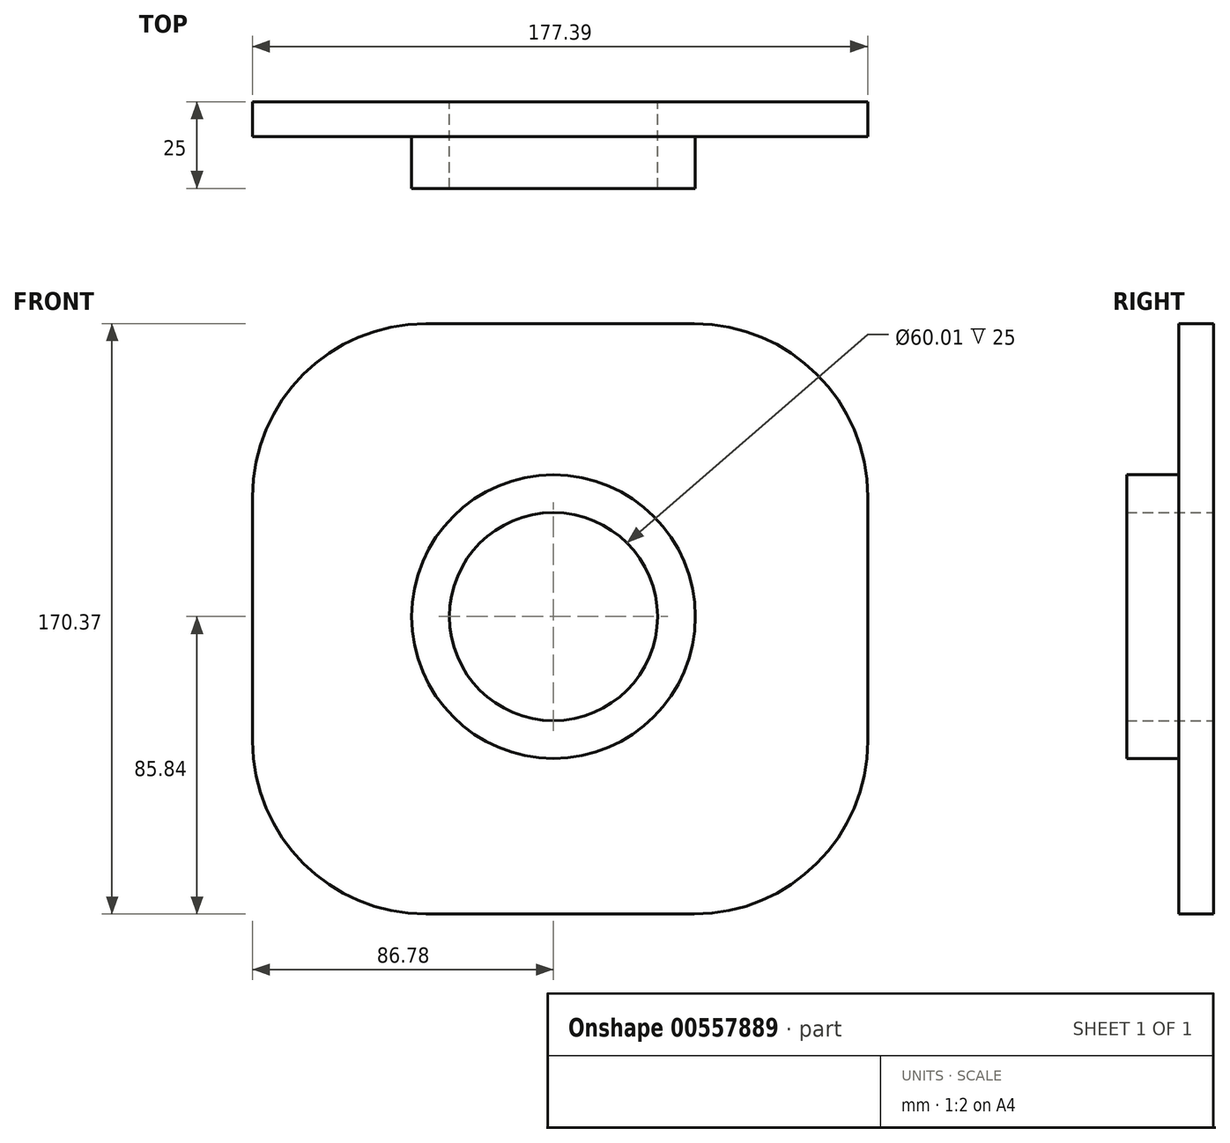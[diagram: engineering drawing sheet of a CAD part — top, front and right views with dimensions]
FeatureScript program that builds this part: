
annotation { "Feature Type Name" : "Feature", "Feature Type Description" : "" }
export const myFeature = defineFeature(function(context is Context, id is Id, definition is map)
    precondition{}
    {
        {
            var Q0;
            Q0=qCreatedBy(makeId("Front.planeOp"),FACE);
            var sketch = newSketch(context, id + "F0", { "sketchPlane" : qUnion([Q0])});
            skLineSegment(sketch, "E0.bottom", {"start": v(-86.78, 84.53) * mm, "end": v(90.6, 84.53) * mm});
            skLineSegment(sketch, "E0.top", {"start": v(-86.78, -85.84) * mm, "end": v(90.6, -85.84) * mm});
            skLineSegment(sketch, "E0.left", {"start": v(-86.78, 84.53) * mm, "end": v(-86.78, -85.84) * mm});
            skLineSegment(sketch, "E0.right", {"start": v(90.6, 84.53) * mm, "end": v(90.6, -85.84) * mm});
            skCircle(sketch, "E1", {"center": v(0, 0) * mm, "radius": 30 * mm});
            skSolve(sketch);
        }
        {
            var Q0;
            Q0=makeQuery(id+"F0.imprint","IMPRINT",FACE,{"disambiguationData":[TD([[makeQuery(id+"F0.imprint","IMPRINT",EDGE,{"derivedFrom":sQuery(id+"F0.wireOp",EDGE,"E0.bottom")}),-1.0]])]});
            extrude(context, id + "F1", {"entities" : qUnion([Q0]), "depth" : 10 * mm, "offsetDistance" : 25 * mm});
        }
        {
            var Q0;
            Q0=makeQuery(id+"F1.opExtrude","CAP_FACE",FACE,{"disambiguationData":[OSD([sQuery(id+"F0.wireOp",EDGE,"E0.bottom"),sQuery(id+"F0.wireOp",EDGE,"E0.top"),sQuery(id+"F0.wireOp",EDGE,"E0.left"),sQuery(id+"F0.wireOp",EDGE,"E0.right"),sQuery(id+"F0.wireOp",EDGE,"E1")])],"isStart":false});
            var sketch = newSketch(context, id + "F2", { "sketchPlane" : qUnion([Q0])});
            skCircle(sketch, "E2.0", {"center": v(0, 0) * mm, "radius": 40.9 * mm});
            skSolve(sketch);
        }
        {
            var Q0;
            Q0=makeQuery(id+"F2.imprint","IMPRINT",FACE,{"disambiguationData":[TD([[makeQuery(id+"F2.imprint","IMPRINT",EDGE,{"derivedFrom":sQuery(id+"F2.wireOp",EDGE,"E2.0")}),1.0]])]});
            extrude(context, id + "F3", {"entities" : qUnion([Q0]), "operationType" : NewBodyOperationType.ADD, "depth" : 15 * mm, "offsetDistance" : 25 * mm});
        }
        {
            var Q0;
            Q0=makeQuery(id+"F1.opExtrude","SWEPT_EDGE",EDGE,{"disambiguationData":[OSD([sQuery(id+"F0.wireOp",EDGE,"E0.bottom"),sQuery(id+"F0.wireOp",EDGE,"E0.left")])]});
            fillet(context, id + "F4", {"entities" : qUnion([Q0]), "radius" : 50 * mm, "tangentPropagation" : true, "allowEdgeOverflow" : false});
        }
        {
            var Q0;
            Q0=makeQuery(id+"F1.opExtrude","SWEPT_EDGE",EDGE,{"disambiguationData":[OSD([sQuery(id+"F0.wireOp",EDGE,"E0.top"),sQuery(id+"F0.wireOp",EDGE,"E0.left")])]});
            var Q1;
            Q1=makeQuery(id+"F1.opExtrude","SWEPT_EDGE",EDGE,{"disambiguationData":[OSD([sQuery(id+"F0.wireOp",EDGE,"E0.top"),sQuery(id+"F0.wireOp",EDGE,"E0.right")])]});
            var Q2;
            Q2=makeQuery(id+"F1.opExtrude","SWEPT_EDGE",EDGE,{"disambiguationData":[OSD([sQuery(id+"F0.wireOp",EDGE,"E0.bottom"),sQuery(id+"F0.wireOp",EDGE,"E0.right")])]});
            fillet(context, id + "F5", {"entities" : qUnion([Q0, Q1, Q2]), "radius" : 50 * mm, "tangentPropagation" : true, "allowEdgeOverflow" : false});
        }
    });
